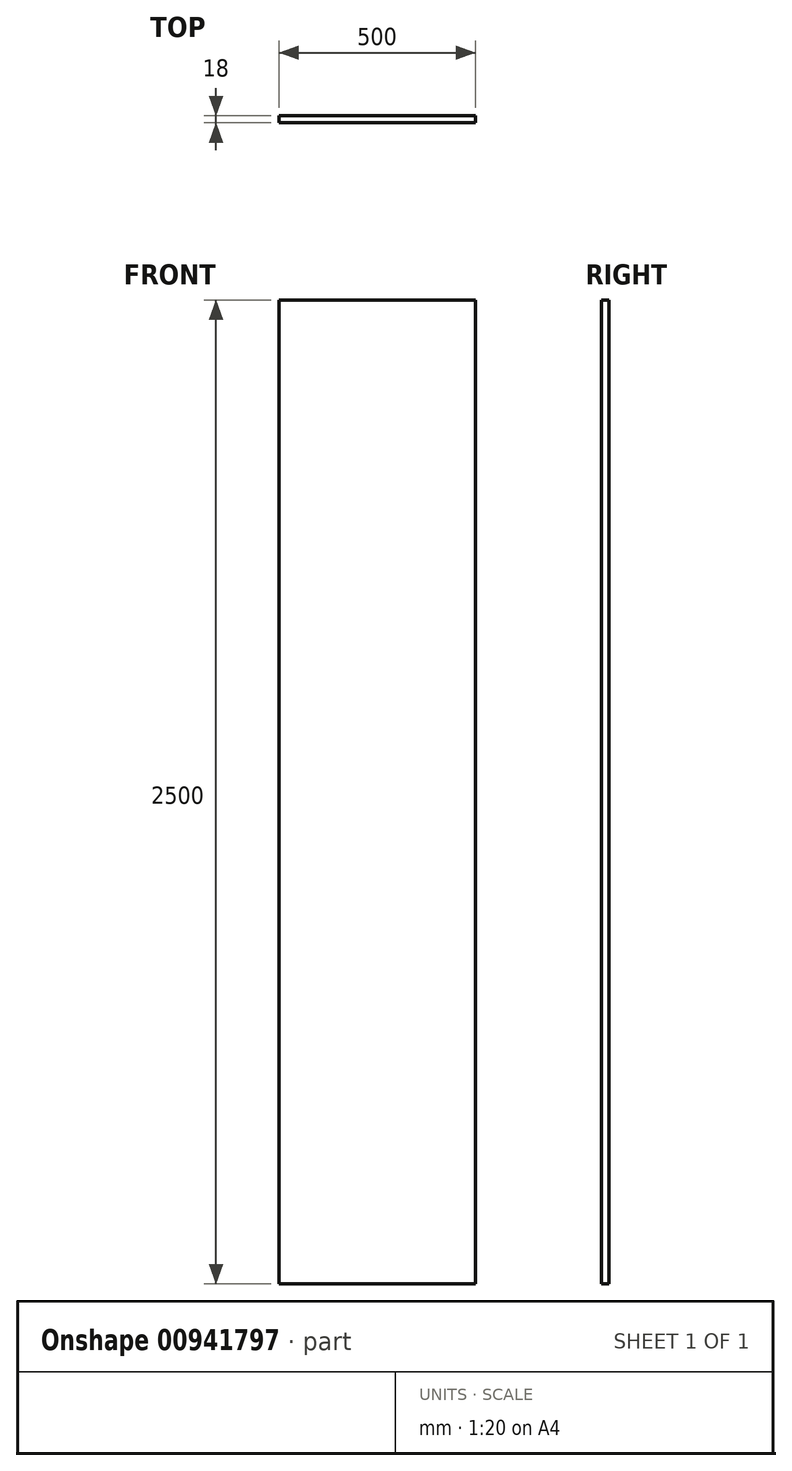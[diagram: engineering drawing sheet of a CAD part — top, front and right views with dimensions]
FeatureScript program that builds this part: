
annotation { "Feature Type Name" : "Feature", "Feature Type Description" : "" }
export const myFeature = defineFeature(function(context is Context, id is Id, definition is map)
    precondition{}
    {
        {
            var Q0;
            Q0=qCreatedBy(makeId("Front.planeOp"),FACE);
            var sketch = newSketch(context, id + "F0", { "sketchPlane" : qUnion([Q0])});
            skLineSegment(sketch, "E0.bottom", {"start": v(250, 1250) * mm, "end": v(-250, 1250) * mm});
            skLineSegment(sketch, "E0.top", {"start": v(250, -1250) * mm, "end": v(-250, -1250) * mm});
            skLineSegment(sketch, "E0.left", {"start": v(250, 1250) * mm, "end": v(250, -1250) * mm});
            skLineSegment(sketch, "E0.right", {"start": v(-250, 1250) * mm, "end": v(-250, -1250) * mm});
            skPoint(sketch, "E0.middle", {"position": v(0, 0) * mm});
            skSolve(sketch);
        }
        {
            var Q0;
            Q0 = qSketchRegion(id + "F0", true);
            extrude(context, id + "F1", {"entities" : qUnion([Q0]), "endBound" : BoundingType.SYMMETRIC, "depth" : 18 * mm, "offsetDistance" : 25 * mm});
        }
    });
